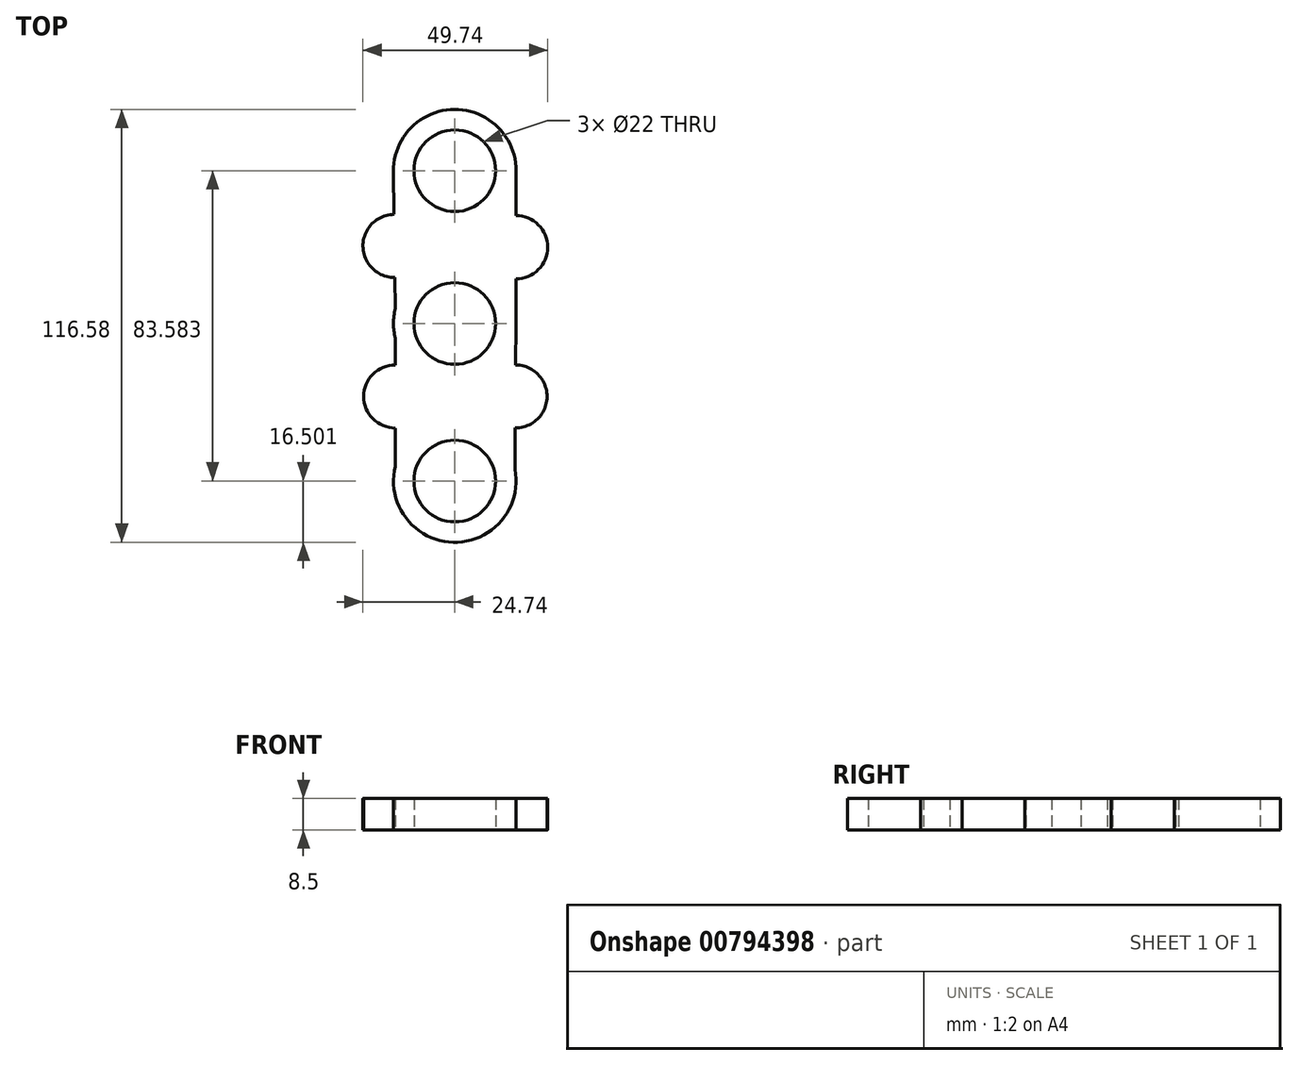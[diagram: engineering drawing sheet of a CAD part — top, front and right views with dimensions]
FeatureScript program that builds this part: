
annotation { "Feature Type Name" : "Feature", "Feature Type Description" : "" }
export const myFeature = defineFeature(function(context is Context, id is Id, definition is map)
    precondition{}
    {
        {
            var Q0;
            Q0=qCreatedBy(makeId("Top.planeOp"),FACE);
            var sketch = newSketch(context, id + "F0", { "sketchPlane" : qUnion([Q0])});
            skCircle(sketch, "E0", {"center": v(0, 0) * mm, "radius": 11 * mm});
            skCircle(sketch, "E1", {"center": v(0, 0) * mm, "radius": 16.5 * mm});
            skCircle(sketch, "E2", {"center": v(0, 41.15) * mm, "radius": 16.5 * mm});
            skCircle(sketch, "E3", {"center": v(0, 41.15) * mm, "radius": 11 * mm});
            skLineSegment(sketch, "E4", {"start": v(-16.5, 40.94) * mm, "end": v(-16.02, 3.97) * mm});
            skLineSegment(sketch, "E5", {"start": v(16.5, 41.08) * mm, "end": v(16.5, 0) * mm});
            skCircle(sketch, "E6", {"center": v(0, -42.43) * mm, "radius": 16.5 * mm});
            skCircle(sketch, "E7", {"center": v(0, -42.43) * mm, "radius": 11 * mm});
            skLineSegment(sketch, "E8", {"start": v(-16.02, 3.97) * mm, "end": v(-16.02, -38.46) * mm});
            skLineSegment(sketch, "E9", {"start": v(16.5, 0) * mm, "end": v(16.2, -39.3) * mm});
            skCircle(sketch, "E10", {"center": v(16.35, -19.65) * mm, "radius": 8.5 * mm});
            skCircle(sketch, "E11", {"center": v(16.5, 20.54) * mm, "radius": 8.5 * mm});
            skCircle(sketch, "E12", {"center": v(-16.24, 20.88) * mm, "radius": 8.5 * mm});
            skCircle(sketch, "E13", {"center": v(-16.02, -19.66) * mm, "radius": 8.5 * mm});
            skSolve(sketch);
        }
        {
            var Q0;
            Q0 = qSketchRegion(id + "F0", true);
            extrude(context, id + "F1", {"entities" : qUnion([Q0]), "depth" : 8.5 * mm, "offsetDistance" : 25 * mm});
        }
    });
